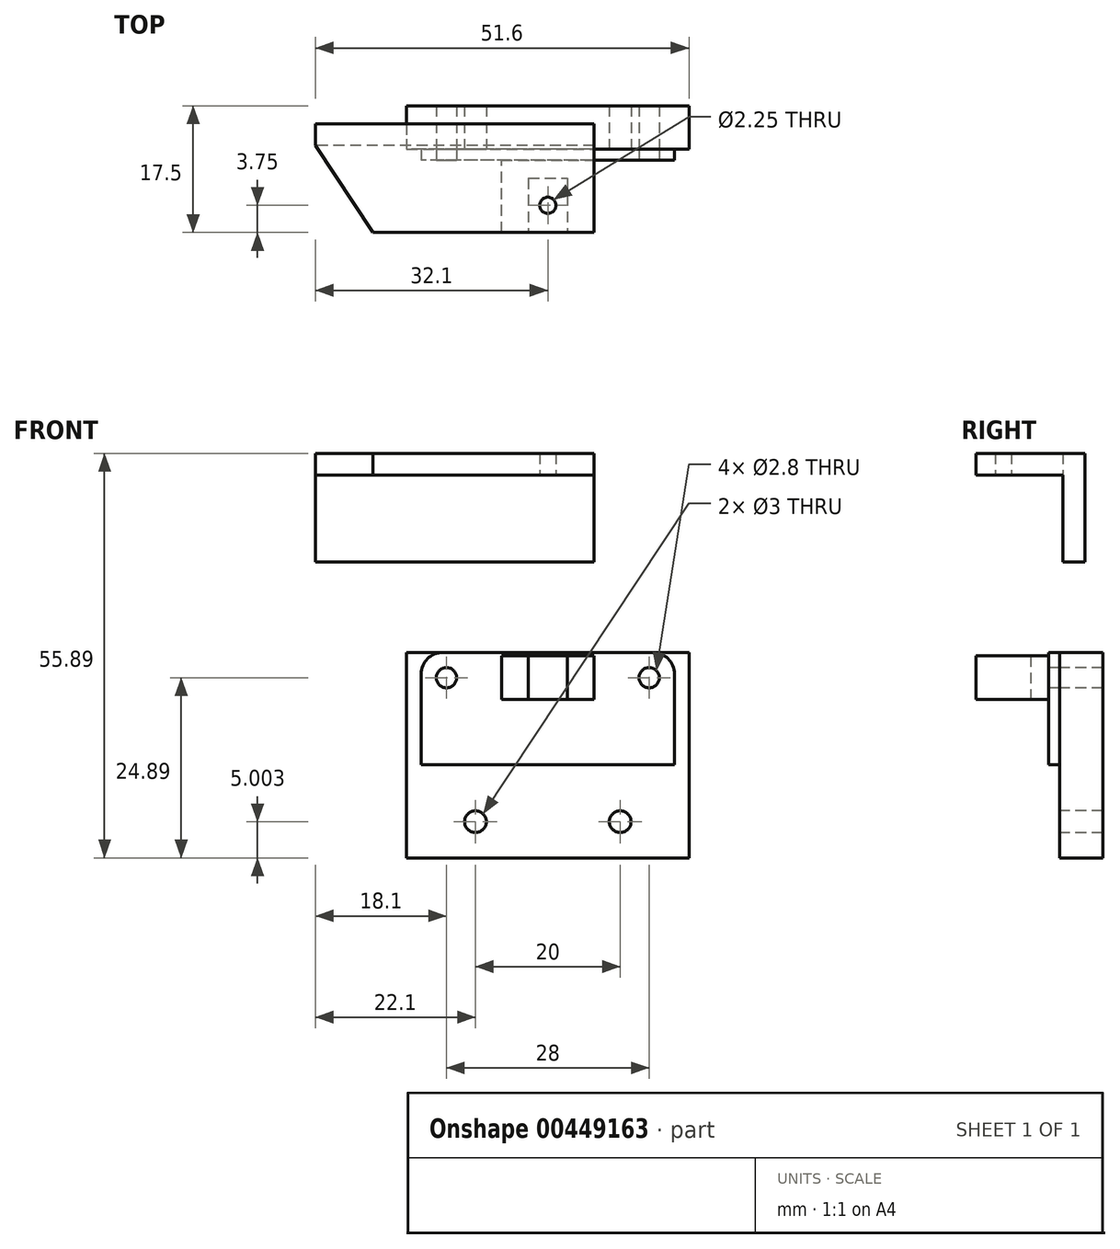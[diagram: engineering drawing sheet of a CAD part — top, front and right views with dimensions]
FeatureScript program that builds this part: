
annotation { "Feature Type Name" : "Feature", "Feature Type Description" : "" }
export const myFeature = defineFeature(function(context is Context, id is Id, definition is map)
    precondition{}
    {
        {
            var Q0;
            Q0=qCreatedBy(makeId("Front.planeOp"),FACE);
            var sketch = newSketch(context, id + "F0", { "sketchPlane" : qUnion([Q0])});
            skLineSegment(sketch, "E0.bottom", {"start": v(14.5, 7.75) * mm, "end": v(-14.5, 7.75) * mm});
            skLineSegment(sketch, "E0.top", {"start": v(17.5, -7.75) * mm, "end": v(-17.5, -7.75) * mm});
            skLineSegment(sketch, "E0.left", {"start": v(17.5, 4.75) * mm, "end": v(17.5, -7.75) * mm});
            skLineSegment(sketch, "E0.right", {"start": v(-17.5, 4.75) * mm, "end": v(-17.5, -7.75) * mm});
            skPoint(sketch, "E0.middle", {"position": v(0, 0) * mm});
            skPoint(sketch, "E1", {"position": v(-17.5, 4.25) * mm});
            skLineSegment(sketch, "E2", {"start": v(-17.5, 4.25) * mm, "end": v(17.5, 4.25) * mm, "construction": true});
            skLineSegment(sketch, "E3.0", {"start": v(-14, 7.75) * mm, "end": v(-14, -7.75) * mm, "construction": true});
            skLineSegment(sketch, "E4.0", {"start": v(14, 7.75) * mm, "end": v(14, -7.75) * mm, "construction": true});
            skCircle(sketch, "E5", {"center": v(14, 4.25) * mm, "radius": 1.4 * mm});
            skCircle(sketch, "E6", {"center": v(-14, 4.25) * mm, "radius": 1.4 * mm});
            skPoint(sketch, "E7.visualSharp", {"position": v(-17.5, 7.75) * mm});
            skArc(sketch, "E7.filletArc", {"start": v(-14.5, 7.75) * mm, "mid": v(-16.62, 6.87) * mm, "end": v(-17.5, 4.75) * mm});
            skPoint(sketch, "E8.visualSharp", {"position": v(17.5, 7.75) * mm});
            skArc(sketch, "E8.filletArc", {"start": v(17.5, 4.75) * mm, "mid": v(16.62, 6.87) * mm, "end": v(14.5, 7.75) * mm});
            skLineSegment(sketch, "E9", {"start": v(0, 4.25) * mm, "end": v(0, 1.25) * mm, "construction": true});
            skPoint(sketch, "E9.endSnap0", {"position": v(0, 4.25) * mm});
            skLineSegment(sketch, "E10", {"start": v(-6.4, 1.25) * mm, "end": v(6.4, 1.25) * mm});
            skLineSegment(sketch, "E11", {"start": v(-6.4, 1.25) * mm, "end": v(-6.4, 4.25) * mm});
            skLineSegment(sketch, "E12", {"start": v(6.4, 1.25) * mm, "end": v(6.4, 4.25) * mm});
            skLineSegment(sketch, "E13.MirrorCS", {"start": v(-6.4, 7.25) * mm, "end": v(6.4, 7.25) * mm});
            skLineSegment(sketch, "E14.MirrorCS", {"start": v(-6.4, 7.25) * mm, "end": v(-6.4, 4.25) * mm});
            skLineSegment(sketch, "E15.MirrorCS", {"start": v(6.4, 7.25) * mm, "end": v(6.4, 4.25) * mm});
            skSolve(sketch);
        }
        {
            var Q0;
            Q0=makeQuery(id+"F0.imprint","IMPRINT",FACE,{"disambiguationData":[TD([[makeQuery(id+"F0.imprint","IMPRINT",EDGE,{"derivedFrom":sQuery(id+"F0.wireOp",EDGE,"E10")}),1.0]])]});
            var Q1;
            Q1=makeQuery(id+"F0.imprint","IMPRINT",FACE,{"disambiguationData":[TD([[makeQuery(id+"F0.imprint","IMPRINT",EDGE,{"derivedFrom":sQuery(id+"F0.wireOp",EDGE,"E0.bottom")}),1.0]])]});
            extrude(context, id + "F1", {"entities" : qUnion([Q0, Q1]), "oppositeDirection" : true, "depth" : 1.5 * mm});
        }
        {
            var Q0;
            Q0=makeQuery(id+"F0.imprint","IMPRINT",FACE,{"disambiguationData":[TD([[makeQuery(id+"F0.imprint","IMPRINT",EDGE,{"derivedFrom":sQuery(id+"F0.wireOp",EDGE,"E10")}),1.0]])]});
            extrude(context, id + "F2", {"entities" : qUnion([Q0]), "operationType" : NewBodyOperationType.ADD, "depth" : 10 * mm});
        }
        {
            var Q0;
            Q0=makeQuery(id+"F2.opExtrude","CAP_FACE",FACE,{"disambiguationData":[OSD([sQuery(id+"F0.wireOp",EDGE,"E10"),sQuery(id+"F0.wireOp",EDGE,"E11"),sQuery(id+"F0.wireOp",EDGE,"E12"),sQuery(id+"F0.wireOp",EDGE,"E13.MirrorCS"),sQuery(id+"F0.wireOp",EDGE,"E14.MirrorCS"),sQuery(id+"F0.wireOp",EDGE,"E15.MirrorCS")])],"isStart":false});
            var sketch = newSketch(context, id + "F3", { "sketchPlane" : qUnion([Q0])});
            skLineSegment(sketch, "E16.0", {"start": v(6.4, 1.25) * mm, "end": v(6.4, 7.25) * mm, "construction": true});
            skLineSegment(sketch, "E17.0", {"start": v(-6.4, 7.25) * mm, "end": v(-6.4, 1.25) * mm, "construction": true});
            skLineSegment(sketch, "E18.0", {"start": v(-2.7, 7.25) * mm, "end": v(-2.7, 1.25) * mm});
            skLineSegment(sketch, "E19.0", {"start": v(2.7, 1.25) * mm, "end": v(2.7, 7.25) * mm});
            skLineSegment(sketch, "E20", {"start": v(-2.7, 7.25) * mm, "end": v(2.7, 7.25) * mm});
            skLineSegment(sketch, "E21", {"start": v(2.7, 1.25) * mm, "end": v(-2.7, 1.25) * mm});
            skSolve(sketch);
        }
        {
            var Q0;
            Q0=makeQuery(id+"F3.imprint","IMPRINT",FACE,{"disambiguationData":[TD([[makeQuery(id+"F3.imprint","IMPRINT",EDGE,{"derivedFrom":sQuery(id+"F3.wireOp",EDGE,"E18.0")}),1.0]])]});
            extrude(context, id + "F4", {"entities" : qUnion([Q0]), "operationType" : NewBodyOperationType.REMOVE, "oppositeDirection" : true, "depth" : 7.5 * mm});
        }
        {
            var Q0;
            Q0=makeQuery(id+"F2.opExtrude","SWEPT_FACE",FACE,{"disambiguationData":[OSD([sQuery(id+"F0.wireOp",EDGE,"E13.MirrorCS")])]});
            cPlane(context, id + "F5", {"entities" : qUnion([Q0]), "cplaneType" : CPlaneType.OFFSET, "offset" : 25 * mm, "width" : 150 * mm, "height" : 150 * mm});
        }
        {
            var Q0;
            Q0=qCreatedBy(id+"F5.planeOp",FACE);
            var sketch = newSketch(context, id + "F6", { "sketchPlane" : qUnion([Q0])});
            skLineSegment(sketch, "E22.0", {"start": v(2.7, -2.5) * mm, "end": v(2.7, -10) * mm, "construction": true});
            skLineSegment(sketch, "E23.0", {"start": v(-2.7, -2.5) * mm, "end": v(-2.7, -10) * mm, "construction": true});
            skLineSegment(sketch, "E24", {"start": v(2.7, -10) * mm, "end": v(-2.7, -2.5) * mm, "construction": true});
            skCircle(sketch, "E25", {"center": v(0, -6.25) * mm, "radius": 1.13 * mm});
            skPoint(sketch, "E26.0", {"position": v(6.4, -10) * mm});
            skLineSegment(sketch, "E27", {"start": v(6.4, -10) * mm, "end": v(6.4, 2) * mm});
            skLineSegment(sketch, "E28", {"start": v(6.4, 2) * mm, "end": v(-32.1, 2) * mm});
            skLineSegment(sketch, "E29", {"start": v(-32.1, 2) * mm, "end": v(-24.15, -10) * mm});
            skLineSegment(sketch, "E30", {"start": v(-24.15, -10) * mm, "end": v(6.4, -10) * mm});
            skLineSegment(sketch, "E31.0", {"start": v(6.4, 5) * mm, "end": v(-32.1, 5) * mm});
            skLineSegment(sketch, "E32", {"start": v(6.4, 5) * mm, "end": v(6.4, 2) * mm});
            skLineSegment(sketch, "E33", {"start": v(-32.1, 5) * mm, "end": v(-32.1, 2) * mm});
            skSolve(sketch);
        }
        {
            var Q0;
            Q0=makeQuery(id+"F6.imprint","IMPRINT",FACE,{"disambiguationData":[TD([[makeQuery(id+"F6.imprint","IMPRINT",EDGE,{"derivedFrom":sQuery(id+"F6.wireOp",EDGE,"E25")}),-1.0]])]});
            var Q1;
            Q1=makeQuery(id+"F6.imprint","IMPRINT",FACE,{"disambiguationData":[TD([[makeQuery(id+"F6.imprint","IMPRINT",EDGE,{"derivedFrom":sQuery(id+"F6.wireOp",EDGE,"E28")}),-1.0]])]});
            extrude(context, id + "F7", {"entities" : qUnion([Q0, Q1]), "depth" : 3 * mm});
        }
        {
            var Q0;
            Q0=makeQuery(id+"F6.imprint","IMPRINT",FACE,{"disambiguationData":[TD([[makeQuery(id+"F6.imprint","IMPRINT",EDGE,{"derivedFrom":sQuery(id+"F6.wireOp",EDGE,"E28")}),-1.0]])]});
            extrude(context, id + "F8", {"entities" : qUnion([Q0]), "operationType" : NewBodyOperationType.ADD, "oppositeDirection" : true, "depth" : 12 * mm});
        }
        {
            var Q0;
            Q0=makeQuery(id+"F1.opExtrude","CAP_FACE",FACE,{"disambiguationData":[OSD([sQuery(id+"F0.wireOp",EDGE,"E0.bottom"),sQuery(id+"F0.wireOp",EDGE,"E0.top"),sQuery(id+"F0.wireOp",EDGE,"E0.left"),sQuery(id+"F0.wireOp",EDGE,"E0.right"),sQuery(id+"F0.wireOp",EDGE,"E5"),sQuery(id+"F0.wireOp",EDGE,"E6"),sQuery(id+"F0.wireOp",EDGE,"E7.filletArc"),sQuery(id+"F0.wireOp",EDGE,"E8.filletArc")])],"isStart":false});
            var sketch = newSketch(context, id + "F9", { "sketchPlane" : qUnion([Q0])});
            skCircle(sketch, "E34.0", {"center": v(-14, 4.25) * mm, "radius": 1.4 * mm});
            skCircle(sketch, "E35.0", {"center": v(14, 4.25) * mm, "radius": 1.4 * mm});
            skLineSegment(sketch, "E36.0", {"start": v(-14.5, 7.75) * mm, "end": v(14.5, 7.75) * mm, "construction": true});
            skLineSegment(sketch, "E37.0", {"start": v(-17.5, -7.75) * mm, "end": v(17.5, -7.75) * mm});
            skLineSegment(sketch, "E38", {"start": v(17.5, -7.75) * mm, "end": v(19.5, -7.75) * mm, "construction": true});
            skLineSegment(sketch, "E39", {"start": v(-17.5, -7.75) * mm, "end": v(-19.5, -7.75) * mm, "construction": true});
            skLineSegment(sketch, "E40", {"start": v(-25.5, 17.25) * mm, "end": v(19.5, 17.25) * mm});
            skLineSegment(sketch, "E41", {"start": v(-19.5, -7.75) * mm, "end": v(-19.5, -20.64) * mm});
            skLineSegment(sketch, "E42", {"start": v(-19.5, -20.64) * mm, "end": v(19.5, -20.64) * mm});
            skLineSegment(sketch, "E43", {"start": v(19.5, -20.64) * mm, "end": v(19.5, -7.75) * mm});
            skLineSegment(sketch, "E44", {"start": v(19.5, -7.75) * mm, "end": v(19.5, 7.75) * mm});
            skLineSegment(sketch, "E45", {"start": v(19.5, 7.75) * mm, "end": v(-19.5, 7.75) * mm});
            skLineSegment(sketch, "E46", {"start": v(-19.5, 7.75) * mm, "end": v(-19.5, -7.75) * mm});
            skLineSegment(sketch, "E47", {"start": v(0, -20.64) * mm, "end": v(0, 7.75) * mm, "construction": true});
            skLineSegment(sketch, "E48", {"start": v(0, -15.64) * mm, "end": v(-10, -15.64) * mm, "construction": true});
            skCircle(sketch, "E49", {"center": v(-10, -15.64) * mm, "radius": 1.5 * mm});
            skCircle(sketch, "E50.MirrorC", {"center": v(10, -15.64) * mm, "radius": 1.5 * mm});
            skSolve(sketch);
        }
        {
            var Q0;
            Q0=makeQuery(id+"F9.imprint","IMPRINT",FACE,{"disambiguationData":[TD([[makeQuery(id+"F9.imprint","IMPRINT",EDGE,{"derivedFrom":sQuery(id+"F9.wireOp",EDGE,"E37.0")}),-1.0]])]});
            var Q1;
            Q1=makeQuery(id+"F9.imprint","IMPRINT",FACE,{"disambiguationData":[TD([[makeQuery(id+"F9.imprint","IMPRINT",EDGE,{"derivedFrom":sQuery(id+"F9.wireOp",EDGE,"E34.0")}),1.0]])]});
            extrude(context, id + "F10", {"entities" : qUnion([Q0, Q1]), "depth" : 6 * mm});
        }
    });
